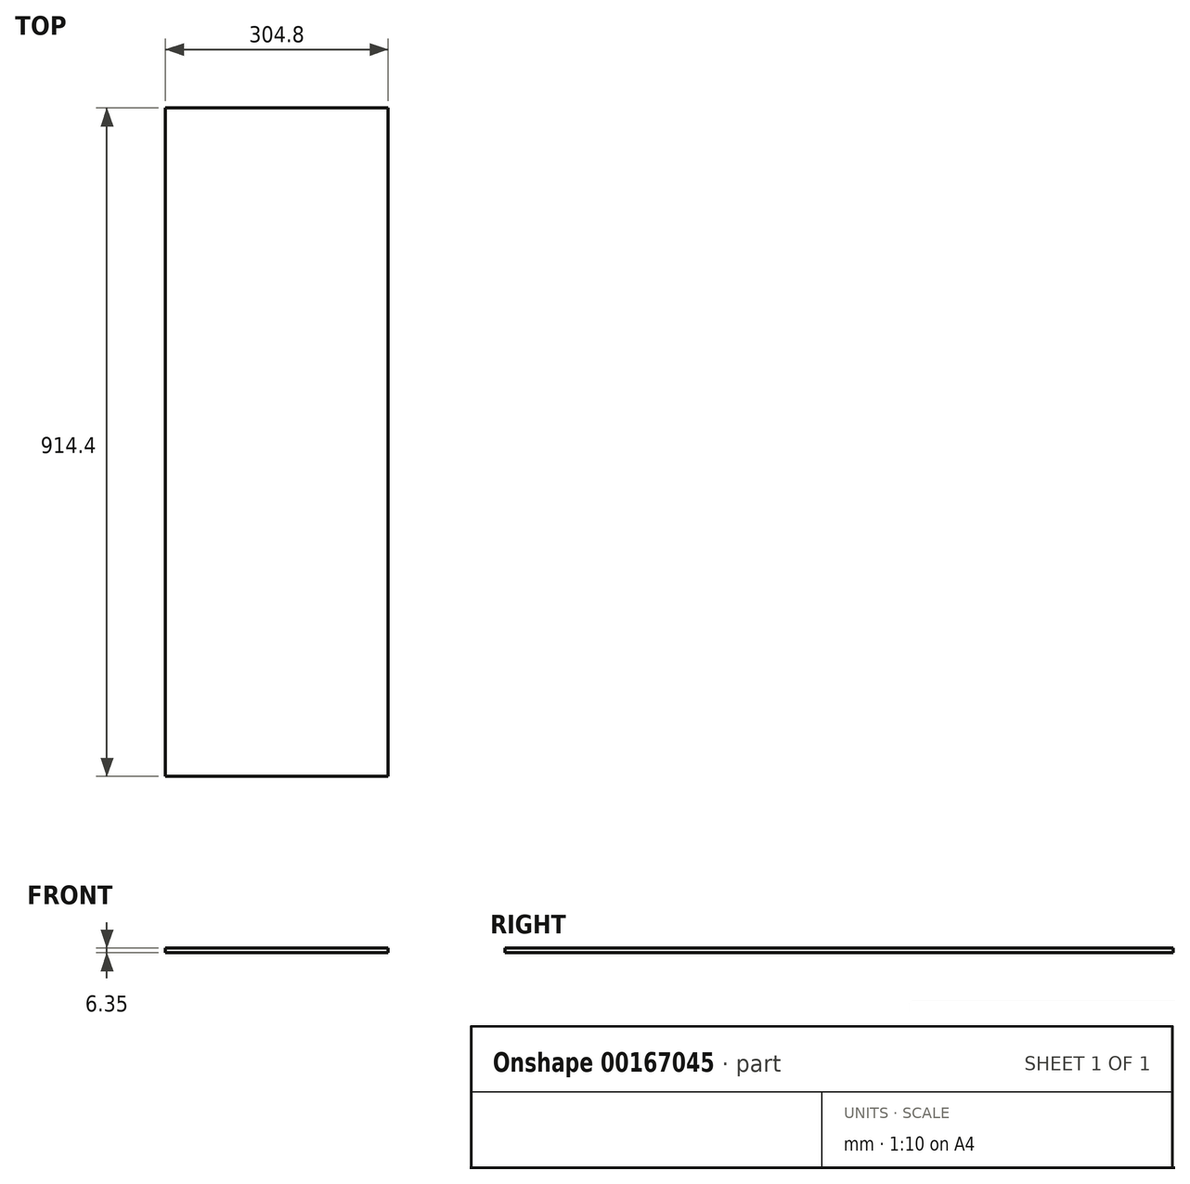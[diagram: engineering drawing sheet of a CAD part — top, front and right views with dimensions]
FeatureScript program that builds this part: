
annotation { "Feature Type Name" : "Feature", "Feature Type Description" : "" }
export const myFeature = defineFeature(function(context is Context, id is Id, definition is map)
    precondition{}
    {
        {
            var Q0;
            Q0=qCreatedBy(makeId("Top.planeOp"),FACE);
            var sketch = newSketch(context, id + "F0", { "sketchPlane" : qUnion([Q0])});
            skLineSegment(sketch, "E0.bottom", {"start": v(0, 0) * mm, "end": v(-304.8, 0) * mm});
            skLineSegment(sketch, "E0.top", {"start": v(0, 914.4) * mm, "end": v(-304.8, 914.4) * mm});
            skLineSegment(sketch, "E0.left", {"start": v(0, 0) * mm, "end": v(0, 914.4) * mm});
            skLineSegment(sketch, "E0.right", {"start": v(-304.8, 0) * mm, "end": v(-304.8, 914.4) * mm});
            skSolve(sketch);
        }
        {
            var Q0;
            Q0=makeQuery(id+"F0.imprint","IMPRINT",FACE,{"disambiguationData":[TD([[makeQuery(id+"F0.imprint","IMPRINT",EDGE,{"derivedFrom":sQuery(id+"F0.wireOp",EDGE,"E0.bottom")}),-1.0]])]});
            extrude(context, id + "F1", {"entities" : qUnion([Q0]), "depth" : 6.35 * mm});
        }
    });
